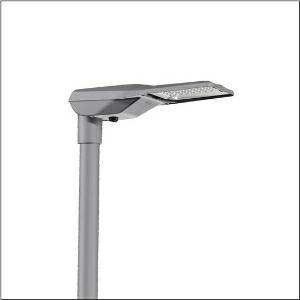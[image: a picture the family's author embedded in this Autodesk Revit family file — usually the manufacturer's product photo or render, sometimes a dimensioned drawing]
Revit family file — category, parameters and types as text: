
# Revit family: streetlight_sl_21_iq_mini___p0_8ab_5xe2r31u08gb_eb08
name_source: partatom
category: Lighting Fixtures
units: mm (PartAtom-declared; Revit-internal decimal feet)

## family parameters
Cut with Voids When Loaded = No
Host = Face
Light Source = No
Part Type = Normal
Room Calculation Point = No
Round Connector Dimension = Use Diameter
Shared = No

## types (1)
- --- (1 x LED, 5200 lm, 39.8 W, 3000K)
    Apparent Load = 40 VA
    CIE Flux Codes = 36 71 98 100 100
    Color Rendering = 70
    Color Temperature = 3000K
    Default Elevation = 1800 mm
    Description = Streetlight SL 21 iQ mini, mast luminaire, primary light control with lens, of PMMA, primary optical cover: cover, of toughened safety glass, transparent, light distribution: P0.8aB, light emission: direct distribution, primary light characteristic: asymmetric, installation type: post-top, side-entry, LED, High Power LED, rated luminous flux: 5.200lm, luminous efficacy: 131lm/W, light colour: 730, colour temperature: 3000K, control gear: iQ-Street Remote, D4i with power reduction, control: pre-setting: logarithmic dimming characteristic, Street-Remote, Auto-Match, Temp-Guard, Lumen-Switch, Night-Set, Smart-Wire, Light-Fading, Desk-Remote (wireless, voltage-free reading and setting of iQ features in the workshop via application-optimized NFC function/RFID function), optimised constant luminous flux control (CLO 2.0), mains connection: 220..240V, AC, 50/60Hz, start of lifetime: 40W, end of service life: 41W, reduction: 18W, luminaire housing, of diecast aluminium, powder-coated, Siteco® metallic grey (DB 702S), corrosivity category C5 mid according to DIN EN ISO 12944, please order mast flange separately, inclination adjustable: 0°, 5°, 10°, 15°, sealing non-destructively replaceable, multi-level sealing system, length: 628mm, width: 235mm, height: 110mm, mast flange for spigot size: 42mm (side-entry): 5XC10008XM4, 60/48mm (side-entry/post-top): 5XC10108XM2, 76/60mm (side-entry/post-top): 5XC10108XM1, mounting height: 4..8m, Smart Interface below, protection rating (complete): IP66, insulation class (complete): insulation class II (safety insulation), certification: CE, ENEC, ENEC+, VDE, impact resistance: IK10, permissible operating ambient temperature for outdoor applications: -40..+50°C, standard-compliant lighting for roads and squares, packaging unit: 1 piece

Light Distribution: P0.8aB
    Height = 110 mm
    Lamp = 1 x LED
    Lamp Light Flux = 5200 lm
    Lamp Power = 39.8 W
    Lamp count = 1
    Length = 625 mm
    Luminous efficacy = 131 lm/W
    Manufacturer = Siteco
    ModVariant = No
    Model = 5XE2R31U08GB
    Number of Poles = 1
    OnlyDefault = Yes
    Power Factor = 1
    Product Name = Streetlight SL 21 iQ mini | P0.8aB
    Product group = mast luminaire | pylon top
    ProductGroupID = 6100
    Protection Class = Protection class II
    Protection Degree = IP 66
    RLX_Detail_Level = 1
    RLX_Emergency_Light_Flux = 0 lm
    RLX_Emergency_Type = 0
    RLX_Emergency_Type_DB = No
    RlxData = <blob elided: 92269 chars, md5=6980a602>
    Socket = socket
    Standby Power = 0 W
    System Light Flux = 5200 lm
    System Power = 40 W
    Type Comments = factory setting: luminous flux: 100 % | dim-lin: 254 | 800 mA
    Type Image = l_1003516.jpg
    URL = http://relux.com
    VarID = @adj_097027
    Voltage = 0 V
    Weight = 0.00 kg
    Width = 234 mm

## geometry (parser evidence)
native form markers: Blend x4, Sweep x9
no freeform markers — native parametric forms only
